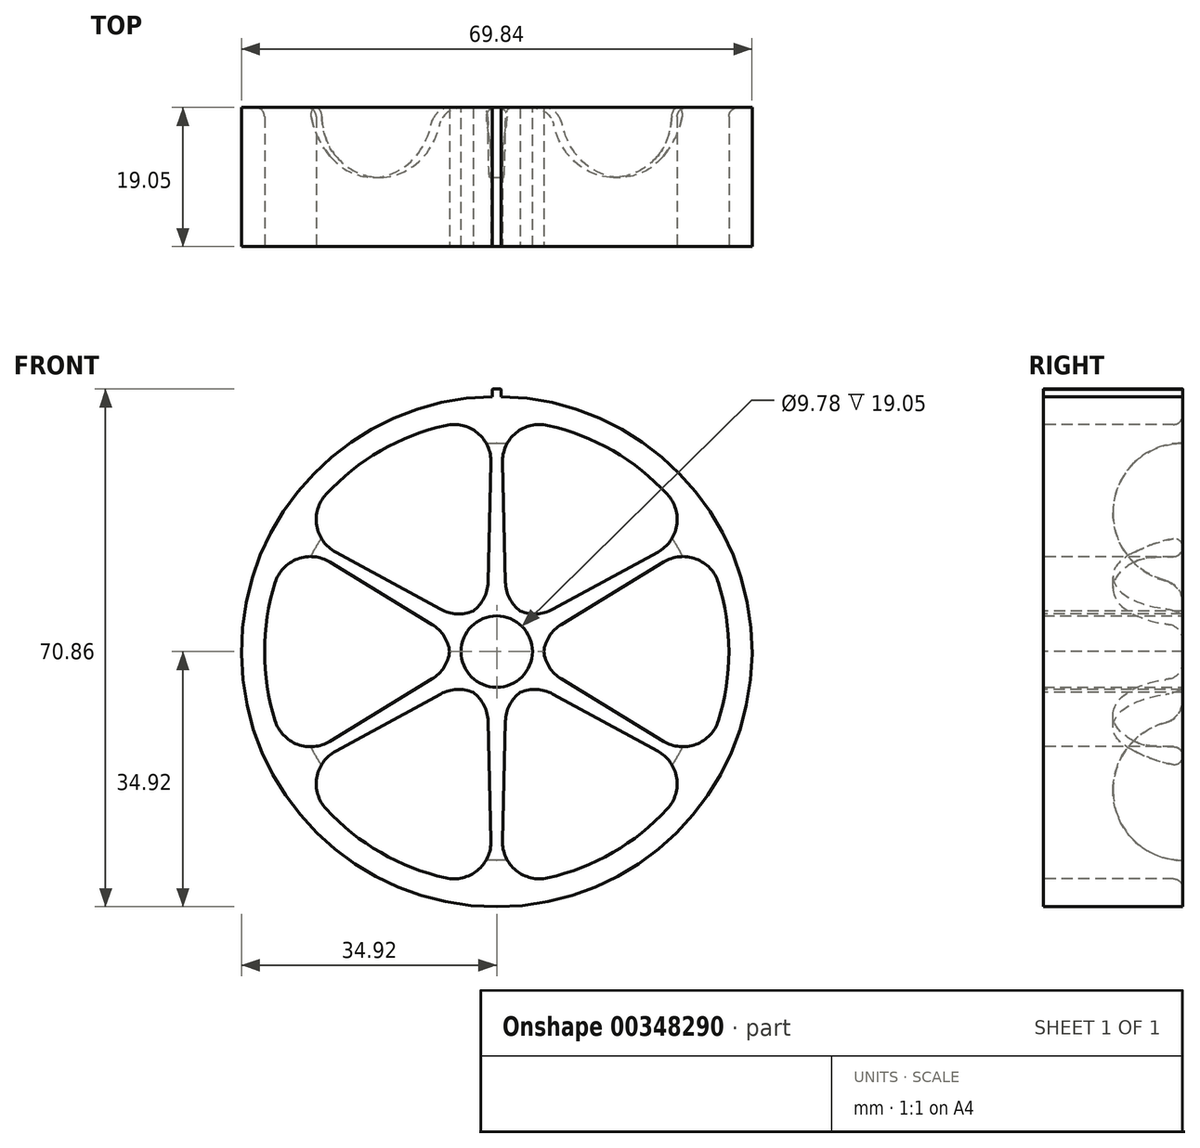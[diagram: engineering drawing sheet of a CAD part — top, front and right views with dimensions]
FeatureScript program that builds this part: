
annotation { "Feature Type Name" : "Feature", "Feature Type Description" : "" }
export const myFeature = defineFeature(function(context is Context, id is Id, definition is map)
    precondition{}
    {
        {
            var Q0;
            Q0=qCreatedBy(makeId("Front.planeOp"),FACE);
            var sketch = newSketch(context, id + "F0", { "sketchPlane" : qUnion([Q0])});
            skCircle(sketch, "E0", {"center": v(0, 0) * mm, "radius": 34.93 * mm});
            skCircle(sketch, "E1", {"center": v(0, 0) * mm, "radius": 4.89 * mm});
            skSolve(sketch);
        }
        {
            var Q0;
            Q0 = qSketchRegion(id + "F0", true);
            extrude(context, id + "F1", {"entities" : qUnion([Q0]), "depth" : 19.05 * mm});
        }
        {
            var Q0;
            Q0=makeQuery(id+"F1.opExtrude","CAP_FACE",FACE,{"disambiguationData":[OSD([sQuery(id+"F0.wireOp",EDGE,"E0"),sQuery(id+"F0.wireOp",EDGE,"E1")])],"isStart":false});
            var sketch = newSketch(context, id + "F2", { "sketchPlane" : qUnion([Q0])});
            skArc(sketch, "E2", {"start": v(-6.08, 2.04) * mm, "mid": v(-6.41, 0) * mm, "end": v(-6.08, -2.04) * mm});
            skArc(sketch, "E3", {"start": v(-0.64, 31.74) * mm, "mid": v(-15.88, 27.5) * mm, "end": v(-27.17, 16.42) * mm});
            skLineSegment(sketch, "E4", {"start": v(0, 0) * mm, "end": v(0, 31.75) * mm, "construction": true});
            skLineSegment(sketch, "E5", {"start": v(-0.64, 31.74) * mm, "end": v(-1.27, 6.29) * mm});
            skLineSegment(sketch, "E6.MirrorCS", {"start": v(0.64, 31.74) * mm, "end": v(1.27, 6.29) * mm});
            skLineSegment(sketch, "E7.1.0", {"start": v(-27.8, 15.32) * mm, "end": v(-6.08, 2.04) * mm});
            skLineSegment(sketch, "E7.1.1", {"start": v(-27.17, 16.42) * mm, "end": v(-4.8, 4.24) * mm});
            skLineSegment(sketch, "E7.2.0", {"start": v(-27.17, -16.42) * mm, "end": v(-4.8, -4.24) * mm});
            skLineSegment(sketch, "E7.2.1", {"start": v(-27.8, -15.32) * mm, "end": v(-6.08, -2.04) * mm});
            skLineSegment(sketch, "E7.3.0", {"start": v(0.63, -31.74) * mm, "end": v(1.27, -6.29) * mm});
            skLineSegment(sketch, "E7.3.1", {"start": v(-0.64, -31.74) * mm, "end": v(-1.27, -6.29) * mm});
            skLineSegment(sketch, "E7.4.0", {"start": v(27.8, -15.32) * mm, "end": v(6.08, -2.04) * mm});
            skLineSegment(sketch, "E7.4.1", {"start": v(27.17, -16.42) * mm, "end": v(4.8, -4.24) * mm});
            skLineSegment(sketch, "E7.5.0", {"start": v(27.17, 16.42) * mm, "end": v(4.8, 4.24) * mm});
            skLineSegment(sketch, "E7.5.1", {"start": v(27.8, 15.32) * mm, "end": v(6.08, 2.04) * mm});
            skArc(sketch, "E8.trimOffspring", {"start": v(-4.8, -4.24) * mm, "mid": v(-3.2, -5.55) * mm, "end": v(-1.27, -6.29) * mm});
            skArc(sketch, "E9.trimOffspring", {"start": v(1.27, -6.29) * mm, "mid": v(3.2, -5.55) * mm, "end": v(4.8, -4.24) * mm});
            skArc(sketch, "E10.trimOffspring", {"start": v(6.08, -2.04) * mm, "mid": v(6.41, 0) * mm, "end": v(6.08, 2.04) * mm});
            skArc(sketch, "E11.trimOffspring", {"start": v(4.8, 4.24) * mm, "mid": v(3.2, 5.55) * mm, "end": v(1.27, 6.29) * mm});
            skArc(sketch, "E12.trimOffspring", {"start": v(-1.27, 6.29) * mm, "mid": v(-3.2, 5.55) * mm, "end": v(-4.8, 4.24) * mm});
            skArc(sketch, "E13.trimOffspring", {"start": v(-27.8, 15.32) * mm, "mid": v(-31.75, 0) * mm, "end": v(-27.8, -15.32) * mm});
            skArc(sketch, "E14.trimOffspring", {"start": v(-27.17, -16.42) * mm, "mid": v(0, -31.75) * mm, "end": v(27.17, -16.42) * mm});
            skArc(sketch, "E15.trimOffspring", {"start": v(27.17, 16.42) * mm, "mid": v(15.87, 27.5) * mm, "end": v(0.63, 31.74) * mm});
            skArc(sketch, "E16.trimOffspring", {"start": v(27.8, -15.32) * mm, "mid": v(31.75, 0) * mm, "end": v(27.8, 15.32) * mm});
            skSolve(sketch);
        }
        {
            var Q0;
            Q0 = qSketchRegion(id + "F2", true);
            extrude(context, id + "F3", {"entities" : qUnion([Q0]), "operationType" : NewBodyOperationType.REMOVE, "endBound" : BoundingType.THROUGH_ALL, "oppositeDirection" : true, "depth" : 25.4 * mm});
        }
        {
            var Q0;
            Q0=qCreatedBy(makeId("Right.planeOp"),FACE);
            var sketch = newSketch(context, id + "F4", { "sketchPlane" : qUnion([Q0])});
            skLineSegment(sketch, "E17.0", {"start": v(0, 31.74) * mm, "end": v(0, 6.29) * mm, "construction": true});
            skArc(sketch, "E18", {"start": v(0, 28.57) * mm, "mid": v(-9.55, 19.02) * mm, "end": v(0, 9.46) * mm});
            skLineSegment(sketch, "E19", {"start": v(0, 28.57) * mm, "end": v(0, 9.46) * mm});
            skSolve(sketch);
        }
        {
            var Q0;
            Q0=qCreatedBy(makeId("Right.planeOp"),FACE);
            var sketch = newSketch(context, id + "F5", { "sketchPlane" : qUnion([Q0])});
            skLineSegment(sketch, "E20", {"start": v(0, 0) * mm, "end": v(-55.17, 0) * mm});
            skSolve(sketch);
        }
        {
            var Q0;
            Q0 = qSketchRegion(id + "F4", true);
            var Q1;
            Q1=sQuery(id+"F5.wireOp",EDGE,"E20");
            revolve(context, id + "F6", {"operationType" : NewBodyOperationType.REMOVE, "entities" : qUnion([Q0]), "axis" : qUnion([Q1]), "revolveType" : RevolveType.FULL, "oppositeDirection" : true});
        }
        {
            var Q0;
            {var subQ0=sQuery(id+"F4.wireOp",EDGE,"E18");var subQ1=sQuery(id+"F4.wireOp",EDGE,"E19");Q0=makeQuery(id+"F6.boolean.opBoolean","COPY",EDGE,{"disambiguationData":[TD([makeQuery(id+"F3.boolean.opBoolean","COPY",FACE,{"derivedFrom":makeQuery(id+"F3.opExtrude","SWEPT_FACE",FACE,{"disambiguationData":[OSD([sQuery(id+"F2.wireOp",EDGE,"E7.4.0")])]})})])],"derivedFrom":makeQuery(id+"F6.opRevolve","SWEPT_EDGE",EDGE,{"disambiguationData":[OSD([subQ0,subQ1]),TDD([makeQuery(id+"F4.imprint","INTERSECT",VERTEX,{"disambiguationData":[OD(0.0)],"derivedFrom":[subQ0,subQ1]})])]})});}
            var Q1;
            {var subQ0=sQuery(id+"F4.wireOp",EDGE,"E18");var subQ1=sQuery(id+"F4.wireOp",EDGE,"E19");Q1=makeQuery(id+"F6.boolean.opBoolean","COPY",EDGE,{"disambiguationData":[TD([makeQuery(id+"F3.boolean.opBoolean","COPY",FACE,{"derivedFrom":makeQuery(id+"F3.opExtrude","SWEPT_FACE",FACE,{"disambiguationData":[OSD([sQuery(id+"F2.wireOp",EDGE,"E7.5.0")])]})})])],"derivedFrom":makeQuery(id+"F6.opRevolve","SWEPT_EDGE",EDGE,{"disambiguationData":[OSD([subQ0,subQ1]),TDD([makeQuery(id+"F4.imprint","INTERSECT",VERTEX,{"disambiguationData":[OD(0.0)],"derivedFrom":[subQ0,subQ1]})])]})});}
            var Q2;
            {var subQ0=sQuery(id+"F4.wireOp",EDGE,"E18");var subQ1=sQuery(id+"F4.wireOp",EDGE,"E19");Q2=makeQuery(id+"F6.boolean.opBoolean","COPY",EDGE,{"disambiguationData":[TD([makeQuery(id+"F3.boolean.opBoolean","COPY",FACE,{"derivedFrom":makeQuery(id+"F3.opExtrude","SWEPT_FACE",FACE,{"disambiguationData":[OSD([sQuery(id+"F2.wireOp",EDGE,"E5")])]})})])],"derivedFrom":makeQuery(id+"F6.opRevolve","SWEPT_EDGE",EDGE,{"disambiguationData":[OSD([subQ0,subQ1]),TDD([makeQuery(id+"F4.imprint","INTERSECT",VERTEX,{"disambiguationData":[OD(0.0)],"derivedFrom":[subQ0,subQ1]})])]})});}
            var Q3;
            {var subQ0=sQuery(id+"F4.wireOp",EDGE,"E18");var subQ1=sQuery(id+"F4.wireOp",EDGE,"E19");Q3=makeQuery(id+"F6.boolean.opBoolean","COPY",EDGE,{"disambiguationData":[TD([makeQuery(id+"F3.boolean.opBoolean","COPY",FACE,{"derivedFrom":makeQuery(id+"F3.opExtrude","SWEPT_FACE",FACE,{"disambiguationData":[OSD([sQuery(id+"F2.wireOp",EDGE,"E7.1.0")])]})})])],"derivedFrom":makeQuery(id+"F6.opRevolve","SWEPT_EDGE",EDGE,{"disambiguationData":[OSD([subQ0,subQ1]),TDD([makeQuery(id+"F4.imprint","INTERSECT",VERTEX,{"disambiguationData":[OD(0.0)],"derivedFrom":[subQ0,subQ1]})])]})});}
            var Q4;
            {var subQ0=sQuery(id+"F4.wireOp",EDGE,"E18");var subQ1=sQuery(id+"F4.wireOp",EDGE,"E19");Q4=makeQuery(id+"F6.boolean.opBoolean","COPY",EDGE,{"disambiguationData":[TD([makeQuery(id+"F3.boolean.opBoolean","COPY",FACE,{"derivedFrom":makeQuery(id+"F3.opExtrude","SWEPT_FACE",FACE,{"disambiguationData":[OSD([sQuery(id+"F2.wireOp",EDGE,"E7.2.0")])]})})])],"derivedFrom":makeQuery(id+"F6.opRevolve","SWEPT_EDGE",EDGE,{"disambiguationData":[OSD([subQ0,subQ1]),TDD([makeQuery(id+"F4.imprint","INTERSECT",VERTEX,{"disambiguationData":[OD(0.0)],"derivedFrom":[subQ0,subQ1]})])]})});}
            var Q5;
            {var subQ0=sQuery(id+"F4.wireOp",EDGE,"E18");var subQ1=sQuery(id+"F4.wireOp",EDGE,"E19");Q5=makeQuery(id+"F6.boolean.opBoolean","COPY",EDGE,{"disambiguationData":[TD([makeQuery(id+"F3.boolean.opBoolean","COPY",FACE,{"derivedFrom":makeQuery(id+"F3.opExtrude","SWEPT_FACE",FACE,{"disambiguationData":[OSD([sQuery(id+"F2.wireOp",EDGE,"E7.3.0")])]})})])],"derivedFrom":makeQuery(id+"F6.opRevolve","SWEPT_EDGE",EDGE,{"disambiguationData":[OSD([subQ0,subQ1]),TDD([makeQuery(id+"F4.imprint","INTERSECT",VERTEX,{"disambiguationData":[OD(0.0)],"derivedFrom":[subQ0,subQ1]})])]})});}
            var Q6;
            {var subQ0=sQuery(id+"F4.wireOp",EDGE,"E18");var subQ1=sQuery(id+"F4.wireOp",EDGE,"E19");Q6=makeQuery(id+"F6.boolean.opBoolean","COPY",EDGE,{"disambiguationData":[TD([makeQuery(id+"F3.boolean.opBoolean","COPY",FACE,{"derivedFrom":makeQuery(id+"F3.opExtrude","SWEPT_FACE",FACE,{"disambiguationData":[OSD([sQuery(id+"F2.wireOp",EDGE,"E7.4.0")])]})})])],"derivedFrom":makeQuery(id+"F6.opRevolve","SWEPT_EDGE",EDGE,{"disambiguationData":[OSD([subQ0,subQ1]),TDD([makeQuery(id+"F4.imprint","INTERSECT",VERTEX,{"disambiguationData":[OD(1.0)],"derivedFrom":[subQ0,subQ1]})])]})});}
            var Q7;
            {var subQ0=sQuery(id+"F4.wireOp",EDGE,"E18");var subQ1=sQuery(id+"F4.wireOp",EDGE,"E19");Q7=makeQuery(id+"F6.boolean.opBoolean","COPY",EDGE,{"disambiguationData":[TD([makeQuery(id+"F3.boolean.opBoolean","COPY",FACE,{"derivedFrom":makeQuery(id+"F3.opExtrude","SWEPT_FACE",FACE,{"disambiguationData":[OSD([sQuery(id+"F2.wireOp",EDGE,"E7.5.0")])]})})])],"derivedFrom":makeQuery(id+"F6.opRevolve","SWEPT_EDGE",EDGE,{"disambiguationData":[OSD([subQ0,subQ1]),TDD([makeQuery(id+"F4.imprint","INTERSECT",VERTEX,{"disambiguationData":[OD(1.0)],"derivedFrom":[subQ0,subQ1]})])]})});}
            var Q8;
            {var subQ0=sQuery(id+"F4.wireOp",EDGE,"E18");var subQ1=sQuery(id+"F4.wireOp",EDGE,"E19");Q8=makeQuery(id+"F6.boolean.opBoolean","COPY",EDGE,{"disambiguationData":[TD([makeQuery(id+"F3.boolean.opBoolean","COPY",FACE,{"derivedFrom":makeQuery(id+"F3.opExtrude","SWEPT_FACE",FACE,{"disambiguationData":[OSD([sQuery(id+"F2.wireOp",EDGE,"E5")])]})})])],"derivedFrom":makeQuery(id+"F6.opRevolve","SWEPT_EDGE",EDGE,{"disambiguationData":[OSD([subQ0,subQ1]),TDD([makeQuery(id+"F4.imprint","INTERSECT",VERTEX,{"disambiguationData":[OD(1.0)],"derivedFrom":[subQ0,subQ1]})])]})});}
            var Q9;
            {var subQ0=sQuery(id+"F4.wireOp",EDGE,"E18");var subQ1=sQuery(id+"F4.wireOp",EDGE,"E19");Q9=makeQuery(id+"F6.boolean.opBoolean","COPY",EDGE,{"disambiguationData":[TD([makeQuery(id+"F3.boolean.opBoolean","COPY",FACE,{"derivedFrom":makeQuery(id+"F3.opExtrude","SWEPT_FACE",FACE,{"disambiguationData":[OSD([sQuery(id+"F2.wireOp",EDGE,"E7.1.0")])]})})])],"derivedFrom":makeQuery(id+"F6.opRevolve","SWEPT_EDGE",EDGE,{"disambiguationData":[OSD([subQ0,subQ1]),TDD([makeQuery(id+"F4.imprint","INTERSECT",VERTEX,{"disambiguationData":[OD(1.0)],"derivedFrom":[subQ0,subQ1]})])]})});}
            var Q10;
            {var subQ0=sQuery(id+"F4.wireOp",EDGE,"E18");var subQ1=sQuery(id+"F4.wireOp",EDGE,"E19");Q10=makeQuery(id+"F6.boolean.opBoolean","COPY",EDGE,{"disambiguationData":[TD([makeQuery(id+"F3.boolean.opBoolean","COPY",FACE,{"derivedFrom":makeQuery(id+"F3.opExtrude","SWEPT_FACE",FACE,{"disambiguationData":[OSD([sQuery(id+"F2.wireOp",EDGE,"E7.2.0")])]})})])],"derivedFrom":makeQuery(id+"F6.opRevolve","SWEPT_EDGE",EDGE,{"disambiguationData":[OSD([subQ0,subQ1]),TDD([makeQuery(id+"F4.imprint","INTERSECT",VERTEX,{"disambiguationData":[OD(1.0)],"derivedFrom":[subQ0,subQ1]})])]})});}
            var Q11;
            {var subQ0=sQuery(id+"F4.wireOp",EDGE,"E18");var subQ1=sQuery(id+"F4.wireOp",EDGE,"E19");Q11=makeQuery(id+"F6.boolean.opBoolean","COPY",EDGE,{"disambiguationData":[TD([makeQuery(id+"F3.boolean.opBoolean","COPY",FACE,{"derivedFrom":makeQuery(id+"F3.opExtrude","SWEPT_FACE",FACE,{"disambiguationData":[OSD([sQuery(id+"F2.wireOp",EDGE,"E7.3.0")])]})})])],"derivedFrom":makeQuery(id+"F6.opRevolve","SWEPT_EDGE",EDGE,{"disambiguationData":[OSD([subQ0,subQ1]),TDD([makeQuery(id+"F4.imprint","INTERSECT",VERTEX,{"disambiguationData":[OD(1.0)],"derivedFrom":[subQ0,subQ1]})])]})});}
            fillet(context, id + "F7", {"entities" : qUnion([Q0, Q1, Q2, Q3, Q4, Q5, Q6, Q7, Q8, Q9, Q10, Q11]), "radius" : 3.17 * mm, "tangentPropagation" : true, "allowEdgeOverflow" : false});
        }
        {
            var Q0;
            Q0=makeQuery(id+"F3.boolean.opBoolean","COPY",EDGE,{"derivedFrom":makeQuery(id+"F3.opExtrude","SWEPT_EDGE",EDGE,{"disambiguationData":[OSD([sQuery(id+"F2.wireOp",EDGE,"E7.5.0"),sQuery(id+"F2.wireOp",EDGE,"E11.trimOffspring")])]})});
            var Q1;
            Q1=makeQuery(id+"F3.boolean.opBoolean","COPY",EDGE,{"derivedFrom":makeQuery(id+"F3.opExtrude","SWEPT_EDGE",EDGE,{"disambiguationData":[OSD([sQuery(id+"F2.wireOp",EDGE,"E7.5.1"),sQuery(id+"F2.wireOp",EDGE,"E10.trimOffspring")])]})});
            var Q2;
            Q2=makeQuery(id+"F3.boolean.opBoolean","COPY",EDGE,{"derivedFrom":makeQuery(id+"F3.opExtrude","SWEPT_EDGE",EDGE,{"disambiguationData":[OSD([sQuery(id+"F2.wireOp",EDGE,"E7.4.0"),sQuery(id+"F2.wireOp",EDGE,"E10.trimOffspring")])]})});
            var Q3;
            Q3=makeQuery(id+"F3.boolean.opBoolean","COPY",EDGE,{"derivedFrom":makeQuery(id+"F3.opExtrude","SWEPT_EDGE",EDGE,{"disambiguationData":[OSD([sQuery(id+"F2.wireOp",EDGE,"E7.4.1"),sQuery(id+"F2.wireOp",EDGE,"E9.trimOffspring")])]})});
            var Q4;
            Q4=makeQuery(id+"F3.boolean.opBoolean","COPY",EDGE,{"derivedFrom":makeQuery(id+"F3.opExtrude","SWEPT_EDGE",EDGE,{"disambiguationData":[OSD([sQuery(id+"F2.wireOp",EDGE,"E7.3.0"),sQuery(id+"F2.wireOp",EDGE,"E9.trimOffspring")])]})});
            var Q5;
            Q5=makeQuery(id+"F3.boolean.opBoolean","COPY",EDGE,{"derivedFrom":makeQuery(id+"F3.opExtrude","SWEPT_EDGE",EDGE,{"disambiguationData":[OSD([sQuery(id+"F2.wireOp",EDGE,"E7.3.1"),sQuery(id+"F2.wireOp",EDGE,"E8.trimOffspring")])]})});
            var Q6;
            Q6=makeQuery(id+"F3.boolean.opBoolean","COPY",EDGE,{"derivedFrom":makeQuery(id+"F3.opExtrude","SWEPT_EDGE",EDGE,{"disambiguationData":[OSD([sQuery(id+"F2.wireOp",EDGE,"E7.2.0"),sQuery(id+"F2.wireOp",EDGE,"E8.trimOffspring")])]})});
            var Q7;
            Q7=makeQuery(id+"F3.boolean.opBoolean","COPY",EDGE,{"derivedFrom":makeQuery(id+"F3.opExtrude","SWEPT_EDGE",EDGE,{"disambiguationData":[OSD([sQuery(id+"F2.wireOp",EDGE,"E2"),sQuery(id+"F2.wireOp",EDGE,"E7.2.1")])]})});
            var Q8;
            Q8=makeQuery(id+"F3.boolean.opBoolean","COPY",EDGE,{"derivedFrom":makeQuery(id+"F3.opExtrude","SWEPT_EDGE",EDGE,{"disambiguationData":[OSD([sQuery(id+"F2.wireOp",EDGE,"E2"),sQuery(id+"F2.wireOp",EDGE,"E7.1.0")])]})});
            var Q9;
            Q9=makeQuery(id+"F3.boolean.opBoolean","COPY",EDGE,{"derivedFrom":makeQuery(id+"F3.opExtrude","SWEPT_EDGE",EDGE,{"disambiguationData":[OSD([sQuery(id+"F2.wireOp",EDGE,"E7.1.1"),sQuery(id+"F2.wireOp",EDGE,"E12.trimOffspring")])]})});
            var Q10;
            Q10=makeQuery(id+"F3.boolean.opBoolean","COPY",EDGE,{"derivedFrom":makeQuery(id+"F3.opExtrude","SWEPT_EDGE",EDGE,{"disambiguationData":[OSD([sQuery(id+"F2.wireOp",EDGE,"E5"),sQuery(id+"F2.wireOp",EDGE,"E12.trimOffspring")])]})});
            var Q11;
            Q11=makeQuery(id+"F3.boolean.opBoolean","COPY",EDGE,{"derivedFrom":makeQuery(id+"F3.opExtrude","SWEPT_EDGE",EDGE,{"disambiguationData":[OSD([sQuery(id+"F2.wireOp",EDGE,"E6.MirrorCS"),sQuery(id+"F2.wireOp",EDGE,"E11.trimOffspring")])]})});
            var Q12;
            Q12=makeQuery(id+"F3.boolean.opBoolean","COPY",EDGE,{"derivedFrom":makeQuery(id+"F3.opExtrude","SWEPT_EDGE",EDGE,{"disambiguationData":[OSD([sQuery(id+"F2.wireOp",EDGE,"E7.4.0"),sQuery(id+"F2.wireOp",EDGE,"E16.trimOffspring")])]})});
            var Q13;
            Q13=makeQuery(id+"F3.boolean.opBoolean","COPY",EDGE,{"derivedFrom":makeQuery(id+"F3.opExtrude","SWEPT_EDGE",EDGE,{"disambiguationData":[OSD([sQuery(id+"F2.wireOp",EDGE,"E7.4.1"),sQuery(id+"F2.wireOp",EDGE,"E14.trimOffspring")])]})});
            var Q14;
            Q14=makeQuery(id+"F3.boolean.opBoolean","COPY",EDGE,{"derivedFrom":makeQuery(id+"F3.opExtrude","SWEPT_EDGE",EDGE,{"disambiguationData":[OSD([sQuery(id+"F2.wireOp",EDGE,"E7.3.0"),sQuery(id+"F2.wireOp",EDGE,"E14.trimOffspring")])]})});
            var Q15;
            Q15=makeQuery(id+"F3.boolean.opBoolean","COPY",EDGE,{"derivedFrom":makeQuery(id+"F3.opExtrude","SWEPT_EDGE",EDGE,{"disambiguationData":[OSD([sQuery(id+"F2.wireOp",EDGE,"E7.3.1"),sQuery(id+"F2.wireOp",EDGE,"E14.trimOffspring")])]})});
            var Q16;
            Q16=makeQuery(id+"F3.boolean.opBoolean","COPY",EDGE,{"derivedFrom":makeQuery(id+"F3.opExtrude","SWEPT_EDGE",EDGE,{"disambiguationData":[OSD([sQuery(id+"F2.wireOp",EDGE,"E7.2.0"),sQuery(id+"F2.wireOp",EDGE,"E14.trimOffspring")])]})});
            var Q17;
            Q17=makeQuery(id+"F3.boolean.opBoolean","COPY",EDGE,{"derivedFrom":makeQuery(id+"F3.opExtrude","SWEPT_EDGE",EDGE,{"disambiguationData":[OSD([sQuery(id+"F2.wireOp",EDGE,"E7.2.1"),sQuery(id+"F2.wireOp",EDGE,"E13.trimOffspring")])]})});
            var Q18;
            Q18=makeQuery(id+"F3.boolean.opBoolean","COPY",EDGE,{"derivedFrom":makeQuery(id+"F3.opExtrude","SWEPT_EDGE",EDGE,{"disambiguationData":[OSD([sQuery(id+"F2.wireOp",EDGE,"E7.1.0"),sQuery(id+"F2.wireOp",EDGE,"E13.trimOffspring")])]})});
            var Q19;
            Q19=makeQuery(id+"F3.boolean.opBoolean","COPY",EDGE,{"derivedFrom":makeQuery(id+"F3.opExtrude","SWEPT_EDGE",EDGE,{"disambiguationData":[OSD([sQuery(id+"F2.wireOp",EDGE,"E3"),sQuery(id+"F2.wireOp",EDGE,"E7.1.1")])]})});
            var Q20;
            Q20=makeQuery(id+"F3.boolean.opBoolean","COPY",EDGE,{"derivedFrom":makeQuery(id+"F3.opExtrude","SWEPT_EDGE",EDGE,{"disambiguationData":[OSD([sQuery(id+"F2.wireOp",EDGE,"E3"),sQuery(id+"F2.wireOp",EDGE,"E5")])]})});
            var Q21;
            Q21=makeQuery(id+"F3.boolean.opBoolean","COPY",EDGE,{"derivedFrom":makeQuery(id+"F3.opExtrude","SWEPT_EDGE",EDGE,{"disambiguationData":[OSD([sQuery(id+"F2.wireOp",EDGE,"E6.MirrorCS"),sQuery(id+"F2.wireOp",EDGE,"E15.trimOffspring")])]})});
            var Q22;
            Q22=makeQuery(id+"F3.boolean.opBoolean","COPY",EDGE,{"derivedFrom":makeQuery(id+"F3.opExtrude","SWEPT_EDGE",EDGE,{"disambiguationData":[OSD([sQuery(id+"F2.wireOp",EDGE,"E7.5.0"),sQuery(id+"F2.wireOp",EDGE,"E15.trimOffspring")])]})});
            var Q23;
            Q23=makeQuery(id+"F3.boolean.opBoolean","COPY",EDGE,{"derivedFrom":makeQuery(id+"F3.opExtrude","SWEPT_EDGE",EDGE,{"disambiguationData":[OSD([sQuery(id+"F2.wireOp",EDGE,"E7.5.1"),sQuery(id+"F2.wireOp",EDGE,"E16.trimOffspring")])]})});
            fillet(context, id + "F8", {"entities" : qUnion([Q0, Q1, Q2, Q3, Q4, Q5, Q6, Q7, Q8, Q9, Q10, Q11, Q12, Q13, Q14, Q15, Q16, Q17, Q18, Q19, Q20, Q21, Q22, Q23]), "radius" : 5.08 * mm, "tangentPropagation" : true, "allowEdgeOverflow" : false});
        }
        {
            var Q0;
            Q0=qCreatedBy(makeId("Right.planeOp"),FACE);
            var sketch = newSketch(context, id + "F9", { "sketchPlane" : qUnion([Q0])});
            skLineSegment(sketch, "E21.0", {"start": v(0, -34.93) * mm, "end": v(0, 34.93) * mm, "construction": true});
            skLineSegment(sketch, "E21.1", {"start": v(-19.05, -34.93) * mm, "end": v(-19.05, 34.93) * mm, "construction": true});
            skLineSegment(sketch, "E22.bottom", {"start": v(0, 34.93) * mm, "end": v(-19.05, 34.93) * mm});
            skLineSegment(sketch, "E22.top", {"start": v(0, 35.94) * mm, "end": v(-19.05, 35.94) * mm});
            skLineSegment(sketch, "E22.left", {"start": v(0, 34.93) * mm, "end": v(0, 35.94) * mm});
            skLineSegment(sketch, "E22.right", {"start": v(-19.05, 34.93) * mm, "end": v(-19.05, 35.94) * mm});
            skSolve(sketch);
        }
        {
            var Q0;
            Q0 = qSketchRegion(id + "F9", true);
            var Q1;
            Q1=sQuery(id+"F5.wireOp",EDGE,"E20");
            revolve(context, id + "F10", {"operationType" : NewBodyOperationType.ADD, "entities" : qUnion([Q0]), "axis" : qUnion([Q1]), "revolveType" : RevolveType.SYMMETRIC, "angle" : 2 * degree});
        }
        {
            var Q0;
            Q0=makeQuery(id+"F3.boolean.opBoolean","INTERSECT",EDGE,{"derivedFrom":[makeQuery(id+"F1.opExtrude","CAP_FACE",FACE,{"disambiguationData":[OSD([sQuery(id+"F0.wireOp",EDGE,"E0"),sQuery(id+"F0.wireOp",EDGE,"E1")])],"isStart":true}),makeQuery(id+"F3.opExtrude","SWEPT_FACE",FACE,{"disambiguationData":[OSD([sQuery(id+"F2.wireOp",EDGE,"E3")])]})]});
            var Q1;
            Q1=makeQuery(id+"F3.boolean.opBoolean","INTERSECT",EDGE,{"derivedFrom":[makeQuery(id+"F1.opExtrude","CAP_FACE",FACE,{"disambiguationData":[OSD([sQuery(id+"F0.wireOp",EDGE,"E0"),sQuery(id+"F0.wireOp",EDGE,"E1")])],"isStart":true}),makeQuery(id+"F3.opExtrude","SWEPT_FACE",FACE,{"disambiguationData":[OSD([sQuery(id+"F2.wireOp",EDGE,"E15.trimOffspring")])]})]});
            var Q2;
            Q2=makeQuery(id+"F3.boolean.opBoolean","INTERSECT",EDGE,{"derivedFrom":[makeQuery(id+"F1.opExtrude","CAP_FACE",FACE,{"disambiguationData":[OSD([sQuery(id+"F0.wireOp",EDGE,"E0"),sQuery(id+"F0.wireOp",EDGE,"E1")])],"isStart":true}),makeQuery(id+"F3.opExtrude","SWEPT_FACE",FACE,{"disambiguationData":[OSD([sQuery(id+"F2.wireOp",EDGE,"E16.trimOffspring")])]})]});
            var Q3;
            {var subQ0=sQuery(id+"F0.wireOp",EDGE,"E1");var subQ1=sQuery(id+"F4.wireOp",EDGE,"E18");var subQ3=makeQuery(id+"F3.boolean.opBoolean","COPY",FACE,{"derivedFrom":makeQuery(id+"F3.opExtrude","SWEPT_FACE",FACE,{"disambiguationData":[OSD([sQuery(id+"F2.wireOp",EDGE,"E7.4.0")])]})});var subQ5=makeQuery(id+"F1.opExtrude","CAP_FACE",FACE,{"disambiguationData":[OSD([sQuery(id+"F0.wireOp",EDGE,"E0"),subQ0])],"isStart":true});var subQ6=sQuery(id+"F4.wireOp",EDGE,"E19");Q3=makeQuery(id+"F7.opFillet","BLEND_EDGE",EDGE,{"blendedFrom":[makeQuery(id+"F6.boolean.opBoolean","COPY",EDGE,{"disambiguationData":[TD([subQ3])],"derivedFrom":makeQuery(id+"F6.opRevolve","SWEPT_EDGE",EDGE,{"disambiguationData":[OSD([subQ1,subQ6]),TDD([makeQuery(id+"F4.imprint","INTERSECT",VERTEX,{"disambiguationData":[OD(1.0)],"derivedFrom":[subQ1,subQ6]})])]})}),makeQuery(id+"F6.boolean.opBoolean","SPLIT",FACE,{"disambiguationData":[TD([makeQuery(id+"F1.opExtrude","SWEPT_FACE",FACE,{"disambiguationData":[OSD([subQ0])]})])],"derivedFrom":subQ5})],"blendedInto":[makeQuery(id+"F6.boolean.opBoolean","SPLIT",FACE,{"disambiguationData":[TD([makeQuery(id+"F1.opExtrude","SWEPT_FACE",FACE,{"disambiguationData":[OSD([subQ0])]})])],"derivedFrom":subQ5})]});}
            var Q4;
            {var subQ0=makeQuery(id+"F3.boolean.opBoolean","COPY",FACE,{"derivedFrom":makeQuery(id+"F3.opExtrude","SWEPT_FACE",FACE,{"disambiguationData":[OSD([sQuery(id+"F2.wireOp",EDGE,"E7.3.0")])]})});var subQ2=sQuery(id+"F0.wireOp",EDGE,"E1");var subQ3=sQuery(id+"F4.wireOp",EDGE,"E18");var subQ5=makeQuery(id+"F1.opExtrude","CAP_FACE",FACE,{"disambiguationData":[OSD([sQuery(id+"F0.wireOp",EDGE,"E0"),subQ2])],"isStart":true});var subQ6=sQuery(id+"F4.wireOp",EDGE,"E19");Q4=makeQuery(id+"F7.opFillet","BLEND_EDGE",EDGE,{"blendedFrom":[makeQuery(id+"F6.boolean.opBoolean","COPY",EDGE,{"disambiguationData":[TD([subQ0])],"derivedFrom":makeQuery(id+"F6.opRevolve","SWEPT_EDGE",EDGE,{"disambiguationData":[OSD([subQ3,subQ6]),TDD([makeQuery(id+"F4.imprint","INTERSECT",VERTEX,{"disambiguationData":[OD(1.0)],"derivedFrom":[subQ3,subQ6]})])]})}),makeQuery(id+"F6.boolean.opBoolean","SPLIT",FACE,{"disambiguationData":[TD([makeQuery(id+"F1.opExtrude","SWEPT_FACE",FACE,{"disambiguationData":[OSD([subQ2])]})])],"derivedFrom":subQ5})],"blendedInto":[makeQuery(id+"F6.boolean.opBoolean","SPLIT",FACE,{"disambiguationData":[TD([makeQuery(id+"F1.opExtrude","SWEPT_FACE",FACE,{"disambiguationData":[OSD([subQ2])]})])],"derivedFrom":subQ5})]});}
            var Q5;
            {var subQ1=makeQuery(id+"F3.boolean.opBoolean","COPY",FACE,{"derivedFrom":makeQuery(id+"F3.opExtrude","SWEPT_FACE",FACE,{"disambiguationData":[OSD([sQuery(id+"F2.wireOp",EDGE,"E7.2.0")])]})});var subQ2=sQuery(id+"F0.wireOp",EDGE,"E1");var subQ3=sQuery(id+"F4.wireOp",EDGE,"E18");var subQ5=makeQuery(id+"F1.opExtrude","CAP_FACE",FACE,{"disambiguationData":[OSD([sQuery(id+"F0.wireOp",EDGE,"E0"),subQ2])],"isStart":true});var subQ6=sQuery(id+"F4.wireOp",EDGE,"E19");Q5=makeQuery(id+"F7.opFillet","BLEND_EDGE",EDGE,{"blendedFrom":[makeQuery(id+"F6.boolean.opBoolean","COPY",EDGE,{"disambiguationData":[TD([subQ1])],"derivedFrom":makeQuery(id+"F6.opRevolve","SWEPT_EDGE",EDGE,{"disambiguationData":[OSD([subQ3,subQ6]),TDD([makeQuery(id+"F4.imprint","INTERSECT",VERTEX,{"disambiguationData":[OD(1.0)],"derivedFrom":[subQ3,subQ6]})])]})}),makeQuery(id+"F6.boolean.opBoolean","SPLIT",FACE,{"disambiguationData":[TD([makeQuery(id+"F1.opExtrude","SWEPT_FACE",FACE,{"disambiguationData":[OSD([subQ2])]})])],"derivedFrom":subQ5})],"blendedInto":[makeQuery(id+"F6.boolean.opBoolean","SPLIT",FACE,{"disambiguationData":[TD([makeQuery(id+"F1.opExtrude","SWEPT_FACE",FACE,{"disambiguationData":[OSD([subQ2])]})])],"derivedFrom":subQ5})]});}
            var Q6;
            {var subQ1=makeQuery(id+"F3.boolean.opBoolean","COPY",FACE,{"derivedFrom":makeQuery(id+"F3.opExtrude","SWEPT_FACE",FACE,{"disambiguationData":[OSD([sQuery(id+"F2.wireOp",EDGE,"E7.1.0")])]})});var subQ2=sQuery(id+"F0.wireOp",EDGE,"E1");var subQ3=sQuery(id+"F4.wireOp",EDGE,"E18");var subQ5=makeQuery(id+"F1.opExtrude","CAP_FACE",FACE,{"disambiguationData":[OSD([sQuery(id+"F0.wireOp",EDGE,"E0"),subQ2])],"isStart":true});var subQ6=sQuery(id+"F4.wireOp",EDGE,"E19");Q6=makeQuery(id+"F7.opFillet","BLEND_EDGE",EDGE,{"blendedFrom":[makeQuery(id+"F6.boolean.opBoolean","COPY",EDGE,{"disambiguationData":[TD([subQ1])],"derivedFrom":makeQuery(id+"F6.opRevolve","SWEPT_EDGE",EDGE,{"disambiguationData":[OSD([subQ3,subQ6]),TDD([makeQuery(id+"F4.imprint","INTERSECT",VERTEX,{"disambiguationData":[OD(1.0)],"derivedFrom":[subQ3,subQ6]})])]})}),makeQuery(id+"F6.boolean.opBoolean","SPLIT",FACE,{"disambiguationData":[TD([makeQuery(id+"F1.opExtrude","SWEPT_FACE",FACE,{"disambiguationData":[OSD([subQ2])]})])],"derivedFrom":subQ5})],"blendedInto":[makeQuery(id+"F6.boolean.opBoolean","SPLIT",FACE,{"disambiguationData":[TD([makeQuery(id+"F1.opExtrude","SWEPT_FACE",FACE,{"disambiguationData":[OSD([subQ2])]})])],"derivedFrom":subQ5})]});}
            var Q7;
            {var subQ0=sQuery(id+"F0.wireOp",EDGE,"E1");var subQ1=sQuery(id+"F4.wireOp",EDGE,"E18");var subQ3=makeQuery(id+"F3.boolean.opBoolean","COPY",FACE,{"derivedFrom":makeQuery(id+"F3.opExtrude","SWEPT_FACE",FACE,{"disambiguationData":[OSD([sQuery(id+"F2.wireOp",EDGE,"E5")])]})});var subQ5=makeQuery(id+"F1.opExtrude","CAP_FACE",FACE,{"disambiguationData":[OSD([sQuery(id+"F0.wireOp",EDGE,"E0"),subQ0])],"isStart":true});var subQ6=sQuery(id+"F4.wireOp",EDGE,"E19");Q7=makeQuery(id+"F7.opFillet","BLEND_EDGE",EDGE,{"blendedFrom":[makeQuery(id+"F6.boolean.opBoolean","COPY",EDGE,{"disambiguationData":[TD([subQ3])],"derivedFrom":makeQuery(id+"F6.opRevolve","SWEPT_EDGE",EDGE,{"disambiguationData":[OSD([subQ1,subQ6]),TDD([makeQuery(id+"F4.imprint","INTERSECT",VERTEX,{"disambiguationData":[OD(1.0)],"derivedFrom":[subQ1,subQ6]})])]})}),makeQuery(id+"F6.boolean.opBoolean","SPLIT",FACE,{"disambiguationData":[TD([makeQuery(id+"F1.opExtrude","SWEPT_FACE",FACE,{"disambiguationData":[OSD([subQ0])]})])],"derivedFrom":subQ5})],"blendedInto":[makeQuery(id+"F6.boolean.opBoolean","SPLIT",FACE,{"disambiguationData":[TD([makeQuery(id+"F1.opExtrude","SWEPT_FACE",FACE,{"disambiguationData":[OSD([subQ0])]})])],"derivedFrom":subQ5})]});}
            var Q8;
            {var subQ0=sQuery(id+"F0.wireOp",EDGE,"E1");var subQ2=sQuery(id+"F4.wireOp",EDGE,"E18");var subQ4=makeQuery(id+"F3.boolean.opBoolean","COPY",FACE,{"derivedFrom":makeQuery(id+"F3.opExtrude","SWEPT_FACE",FACE,{"disambiguationData":[OSD([sQuery(id+"F2.wireOp",EDGE,"E7.5.0")])]})});var subQ5=makeQuery(id+"F1.opExtrude","CAP_FACE",FACE,{"disambiguationData":[OSD([sQuery(id+"F0.wireOp",EDGE,"E0"),subQ0])],"isStart":true});var subQ6=sQuery(id+"F4.wireOp",EDGE,"E19");Q8=makeQuery(id+"F7.opFillet","BLEND_EDGE",EDGE,{"blendedFrom":[makeQuery(id+"F6.boolean.opBoolean","COPY",EDGE,{"disambiguationData":[TD([subQ4])],"derivedFrom":makeQuery(id+"F6.opRevolve","SWEPT_EDGE",EDGE,{"disambiguationData":[OSD([subQ2,subQ6]),TDD([makeQuery(id+"F4.imprint","INTERSECT",VERTEX,{"disambiguationData":[OD(1.0)],"derivedFrom":[subQ2,subQ6]})])]})}),makeQuery(id+"F6.boolean.opBoolean","SPLIT",FACE,{"disambiguationData":[TD([makeQuery(id+"F1.opExtrude","SWEPT_FACE",FACE,{"disambiguationData":[OSD([subQ0])]})])],"derivedFrom":subQ5})],"blendedInto":[makeQuery(id+"F6.boolean.opBoolean","SPLIT",FACE,{"disambiguationData":[TD([makeQuery(id+"F1.opExtrude","SWEPT_FACE",FACE,{"disambiguationData":[OSD([subQ0])]})])],"derivedFrom":subQ5})]});}
            var Q9;
            {var subQ0=sQuery(id+"F2.wireOp",EDGE,"E14.trimOffspring");Q9=makeQuery(id+"F3.boolean.opBoolean","INTERSECT",EDGE,{"derivedFrom":[makeQuery(id+"F1.opExtrude","CAP_FACE",FACE,{"disambiguationData":[OSD([sQuery(id+"F0.wireOp",EDGE,"E0"),sQuery(id+"F0.wireOp",EDGE,"E1")])],"isStart":true}),makeQuery(id+"F3.opExtrude","SWEPT_FACE",FACE,{"disambiguationData":[OSD([subQ0]),TDD([makeQuery(id+"F2.imprint","IMPRINT",EDGE,{"disambiguationData":[TD([[makeQuery(id+"F2.imprint","INTERSECT",VERTEX,{"derivedFrom":[sQuery(id+"F2.wireOp",EDGE,"E7.3.0"),subQ0]}),-1.0]])],"derivedFrom":subQ0})])]})]});}
            var Q10;
            {var subQ2=sQuery(id+"F2.wireOp",EDGE,"E7.3.0");var subQ3=makeQuery(id+"F3.boolean.opBoolean","COPY",FACE,{"derivedFrom":makeQuery(id+"F3.opExtrude","SWEPT_FACE",FACE,{"disambiguationData":[OSD([subQ2])]})});var subQ5=sQuery(id+"F0.wireOp",EDGE,"E0");var subQ7=sQuery(id+"F4.wireOp",EDGE,"E18");var subQ10=makeQuery(id+"F1.opExtrude","CAP_FACE",FACE,{"disambiguationData":[OSD([subQ5,sQuery(id+"F0.wireOp",EDGE,"E1")])],"isStart":true});var subQ11=sQuery(id+"F4.wireOp",EDGE,"E19");Q10=makeQuery(id+"F7.opFillet","BLEND_EDGE",EDGE,{"blendedFrom":[makeQuery(id+"F6.boolean.opBoolean","COPY",EDGE,{"disambiguationData":[TD([subQ3])],"derivedFrom":makeQuery(id+"F6.opRevolve","SWEPT_EDGE",EDGE,{"disambiguationData":[OSD([subQ7,subQ11]),TDD([makeQuery(id+"F4.imprint","INTERSECT",VERTEX,{"disambiguationData":[OD(0.0)],"derivedFrom":[subQ7,subQ11]})])]})}),makeQuery(id+"F6.boolean.opBoolean","SPLIT",FACE,{"disambiguationData":[TD([makeQuery(id+"F1.opExtrude","SWEPT_FACE",FACE,{"disambiguationData":[OSD([subQ5])]})])],"derivedFrom":subQ10})],"blendedInto":[makeQuery(id+"F6.boolean.opBoolean","SPLIT",FACE,{"disambiguationData":[TD([makeQuery(id+"F1.opExtrude","SWEPT_FACE",FACE,{"disambiguationData":[OSD([subQ5])]})])],"derivedFrom":subQ10})]});}
            var Q11;
            {var subQ0=sQuery(id+"F2.wireOp",EDGE,"E14.trimOffspring");Q11=makeQuery(id+"F3.boolean.opBoolean","INTERSECT",EDGE,{"derivedFrom":[makeQuery(id+"F1.opExtrude","CAP_FACE",FACE,{"disambiguationData":[OSD([sQuery(id+"F0.wireOp",EDGE,"E0"),sQuery(id+"F0.wireOp",EDGE,"E1")])],"isStart":true}),makeQuery(id+"F3.opExtrude","SWEPT_FACE",FACE,{"disambiguationData":[OSD([subQ0]),TDD([makeQuery(id+"F2.imprint","IMPRINT",EDGE,{"disambiguationData":[TD([[makeQuery(id+"F2.imprint","INTERSECT",VERTEX,{"derivedFrom":[sQuery(id+"F2.wireOp",EDGE,"E7.2.0"),subQ0]}),-1.0]])],"derivedFrom":subQ0})])]})]});}
            var Q12;
            Q12=makeQuery(id+"F3.boolean.opBoolean","INTERSECT",EDGE,{"derivedFrom":[makeQuery(id+"F1.opExtrude","CAP_FACE",FACE,{"disambiguationData":[OSD([sQuery(id+"F0.wireOp",EDGE,"E0"),sQuery(id+"F0.wireOp",EDGE,"E1")])],"isStart":true}),makeQuery(id+"F3.opExtrude","SWEPT_FACE",FACE,{"disambiguationData":[OSD([sQuery(id+"F2.wireOp",EDGE,"E13.trimOffspring")])]})]});
            var Q13;
            {var subQ3=sQuery(id+"F2.wireOp",EDGE,"E7.2.0");var subQ4=makeQuery(id+"F3.boolean.opBoolean","COPY",FACE,{"derivedFrom":makeQuery(id+"F3.opExtrude","SWEPT_FACE",FACE,{"disambiguationData":[OSD([subQ3])]})});var subQ5=sQuery(id+"F0.wireOp",EDGE,"E0");var subQ7=sQuery(id+"F4.wireOp",EDGE,"E18");var subQ10=makeQuery(id+"F1.opExtrude","CAP_FACE",FACE,{"disambiguationData":[OSD([subQ5,sQuery(id+"F0.wireOp",EDGE,"E1")])],"isStart":true});var subQ11=sQuery(id+"F4.wireOp",EDGE,"E19");Q13=makeQuery(id+"F7.opFillet","BLEND_EDGE",EDGE,{"blendedFrom":[makeQuery(id+"F6.boolean.opBoolean","COPY",EDGE,{"disambiguationData":[TD([subQ4])],"derivedFrom":makeQuery(id+"F6.opRevolve","SWEPT_EDGE",EDGE,{"disambiguationData":[OSD([subQ7,subQ11]),TDD([makeQuery(id+"F4.imprint","INTERSECT",VERTEX,{"disambiguationData":[OD(0.0)],"derivedFrom":[subQ7,subQ11]})])]})}),makeQuery(id+"F6.boolean.opBoolean","SPLIT",FACE,{"disambiguationData":[TD([makeQuery(id+"F1.opExtrude","SWEPT_FACE",FACE,{"disambiguationData":[OSD([subQ5])]})])],"derivedFrom":subQ10})],"blendedInto":[makeQuery(id+"F6.boolean.opBoolean","SPLIT",FACE,{"disambiguationData":[TD([makeQuery(id+"F1.opExtrude","SWEPT_FACE",FACE,{"disambiguationData":[OSD([subQ5])]})])],"derivedFrom":subQ10})]});}
            var Q14;
            {var subQ3=makeQuery(id+"F3.boolean.opBoolean","COPY",FACE,{"derivedFrom":makeQuery(id+"F3.opExtrude","SWEPT_FACE",FACE,{"disambiguationData":[OSD([sQuery(id+"F2.wireOp",EDGE,"E7.1.0")])]})});var subQ5=sQuery(id+"F0.wireOp",EDGE,"E0");var subQ7=sQuery(id+"F4.wireOp",EDGE,"E18");var subQ10=makeQuery(id+"F1.opExtrude","CAP_FACE",FACE,{"disambiguationData":[OSD([subQ5,sQuery(id+"F0.wireOp",EDGE,"E1")])],"isStart":true});var subQ11=sQuery(id+"F4.wireOp",EDGE,"E19");Q14=makeQuery(id+"F7.opFillet","BLEND_EDGE",EDGE,{"blendedFrom":[makeQuery(id+"F6.boolean.opBoolean","COPY",EDGE,{"disambiguationData":[TD([subQ3])],"derivedFrom":makeQuery(id+"F6.opRevolve","SWEPT_EDGE",EDGE,{"disambiguationData":[OSD([subQ7,subQ11]),TDD([makeQuery(id+"F4.imprint","INTERSECT",VERTEX,{"disambiguationData":[OD(0.0)],"derivedFrom":[subQ7,subQ11]})])]})}),makeQuery(id+"F6.boolean.opBoolean","SPLIT",FACE,{"disambiguationData":[TD([makeQuery(id+"F1.opExtrude","SWEPT_FACE",FACE,{"disambiguationData":[OSD([subQ5])]})])],"derivedFrom":subQ10})],"blendedInto":[makeQuery(id+"F6.boolean.opBoolean","SPLIT",FACE,{"disambiguationData":[TD([makeQuery(id+"F1.opExtrude","SWEPT_FACE",FACE,{"disambiguationData":[OSD([subQ5])]})])],"derivedFrom":subQ10})]});}
            var Q15;
            {var subQ3=sQuery(id+"F0.wireOp",EDGE,"E0");var subQ4=makeQuery(id+"F3.boolean.opBoolean","COPY",FACE,{"derivedFrom":makeQuery(id+"F3.opExtrude","SWEPT_FACE",FACE,{"disambiguationData":[OSD([sQuery(id+"F2.wireOp",EDGE,"E5")])]})});var subQ7=sQuery(id+"F4.wireOp",EDGE,"E18");var subQ10=makeQuery(id+"F1.opExtrude","CAP_FACE",FACE,{"disambiguationData":[OSD([subQ3,sQuery(id+"F0.wireOp",EDGE,"E1")])],"isStart":true});var subQ11=sQuery(id+"F4.wireOp",EDGE,"E19");Q15=makeQuery(id+"F7.opFillet","BLEND_EDGE",EDGE,{"blendedFrom":[makeQuery(id+"F6.boolean.opBoolean","COPY",EDGE,{"disambiguationData":[TD([subQ4])],"derivedFrom":makeQuery(id+"F6.opRevolve","SWEPT_EDGE",EDGE,{"disambiguationData":[OSD([subQ7,subQ11]),TDD([makeQuery(id+"F4.imprint","INTERSECT",VERTEX,{"disambiguationData":[OD(0.0)],"derivedFrom":[subQ7,subQ11]})])]})}),makeQuery(id+"F6.boolean.opBoolean","SPLIT",FACE,{"disambiguationData":[TD([makeQuery(id+"F1.opExtrude","SWEPT_FACE",FACE,{"disambiguationData":[OSD([subQ3])]})])],"derivedFrom":subQ10})],"blendedInto":[makeQuery(id+"F6.boolean.opBoolean","SPLIT",FACE,{"disambiguationData":[TD([makeQuery(id+"F1.opExtrude","SWEPT_FACE",FACE,{"disambiguationData":[OSD([subQ3])]})])],"derivedFrom":subQ10})]});}
            var Q16;
            {var subQ3=sQuery(id+"F0.wireOp",EDGE,"E0");var subQ5=makeQuery(id+"F3.boolean.opBoolean","COPY",FACE,{"derivedFrom":makeQuery(id+"F3.opExtrude","SWEPT_FACE",FACE,{"disambiguationData":[OSD([sQuery(id+"F2.wireOp",EDGE,"E7.5.0")])]})});var subQ7=sQuery(id+"F4.wireOp",EDGE,"E18");var subQ10=makeQuery(id+"F1.opExtrude","CAP_FACE",FACE,{"disambiguationData":[OSD([subQ3,sQuery(id+"F0.wireOp",EDGE,"E1")])],"isStart":true});var subQ11=sQuery(id+"F4.wireOp",EDGE,"E19");Q16=makeQuery(id+"F7.opFillet","BLEND_EDGE",EDGE,{"blendedFrom":[makeQuery(id+"F6.boolean.opBoolean","COPY",EDGE,{"disambiguationData":[TD([subQ5])],"derivedFrom":makeQuery(id+"F6.opRevolve","SWEPT_EDGE",EDGE,{"disambiguationData":[OSD([subQ7,subQ11]),TDD([makeQuery(id+"F4.imprint","INTERSECT",VERTEX,{"disambiguationData":[OD(0.0)],"derivedFrom":[subQ7,subQ11]})])]})}),makeQuery(id+"F6.boolean.opBoolean","SPLIT",FACE,{"disambiguationData":[TD([makeQuery(id+"F1.opExtrude","SWEPT_FACE",FACE,{"disambiguationData":[OSD([subQ3])]})])],"derivedFrom":subQ10})],"blendedInto":[makeQuery(id+"F6.boolean.opBoolean","SPLIT",FACE,{"disambiguationData":[TD([makeQuery(id+"F1.opExtrude","SWEPT_FACE",FACE,{"disambiguationData":[OSD([subQ3])]})])],"derivedFrom":subQ10})]});}
            var Q17;
            {var subQ3=sQuery(id+"F0.wireOp",EDGE,"E0");var subQ4=makeQuery(id+"F3.boolean.opBoolean","COPY",FACE,{"derivedFrom":makeQuery(id+"F3.opExtrude","SWEPT_FACE",FACE,{"disambiguationData":[OSD([sQuery(id+"F2.wireOp",EDGE,"E7.4.0")])]})});var subQ7=sQuery(id+"F4.wireOp",EDGE,"E18");var subQ10=makeQuery(id+"F1.opExtrude","CAP_FACE",FACE,{"disambiguationData":[OSD([subQ3,sQuery(id+"F0.wireOp",EDGE,"E1")])],"isStart":true});var subQ11=sQuery(id+"F4.wireOp",EDGE,"E19");Q17=makeQuery(id+"F7.opFillet","BLEND_EDGE",EDGE,{"blendedFrom":[makeQuery(id+"F6.boolean.opBoolean","COPY",EDGE,{"disambiguationData":[TD([subQ4])],"derivedFrom":makeQuery(id+"F6.opRevolve","SWEPT_EDGE",EDGE,{"disambiguationData":[OSD([subQ7,subQ11]),TDD([makeQuery(id+"F4.imprint","INTERSECT",VERTEX,{"disambiguationData":[OD(0.0)],"derivedFrom":[subQ7,subQ11]})])]})}),makeQuery(id+"F6.boolean.opBoolean","SPLIT",FACE,{"disambiguationData":[TD([makeQuery(id+"F1.opExtrude","SWEPT_FACE",FACE,{"disambiguationData":[OSD([subQ3])]})])],"derivedFrom":subQ10})],"blendedInto":[makeQuery(id+"F6.boolean.opBoolean","SPLIT",FACE,{"disambiguationData":[TD([makeQuery(id+"F1.opExtrude","SWEPT_FACE",FACE,{"disambiguationData":[OSD([subQ3])]})])],"derivedFrom":subQ10})]});}
            fillet(context, id + "F11", {"entities" : qUnion([Q0, Q1, Q2, Q3, Q4, Q5, Q6, Q7, Q8, Q9, Q10, Q11, Q12, Q13, Q14, Q15, Q16, Q17]), "radius" : 1.27 * mm, "tangentPropagation" : true, "allowEdgeOverflow" : false});
        }
    });
